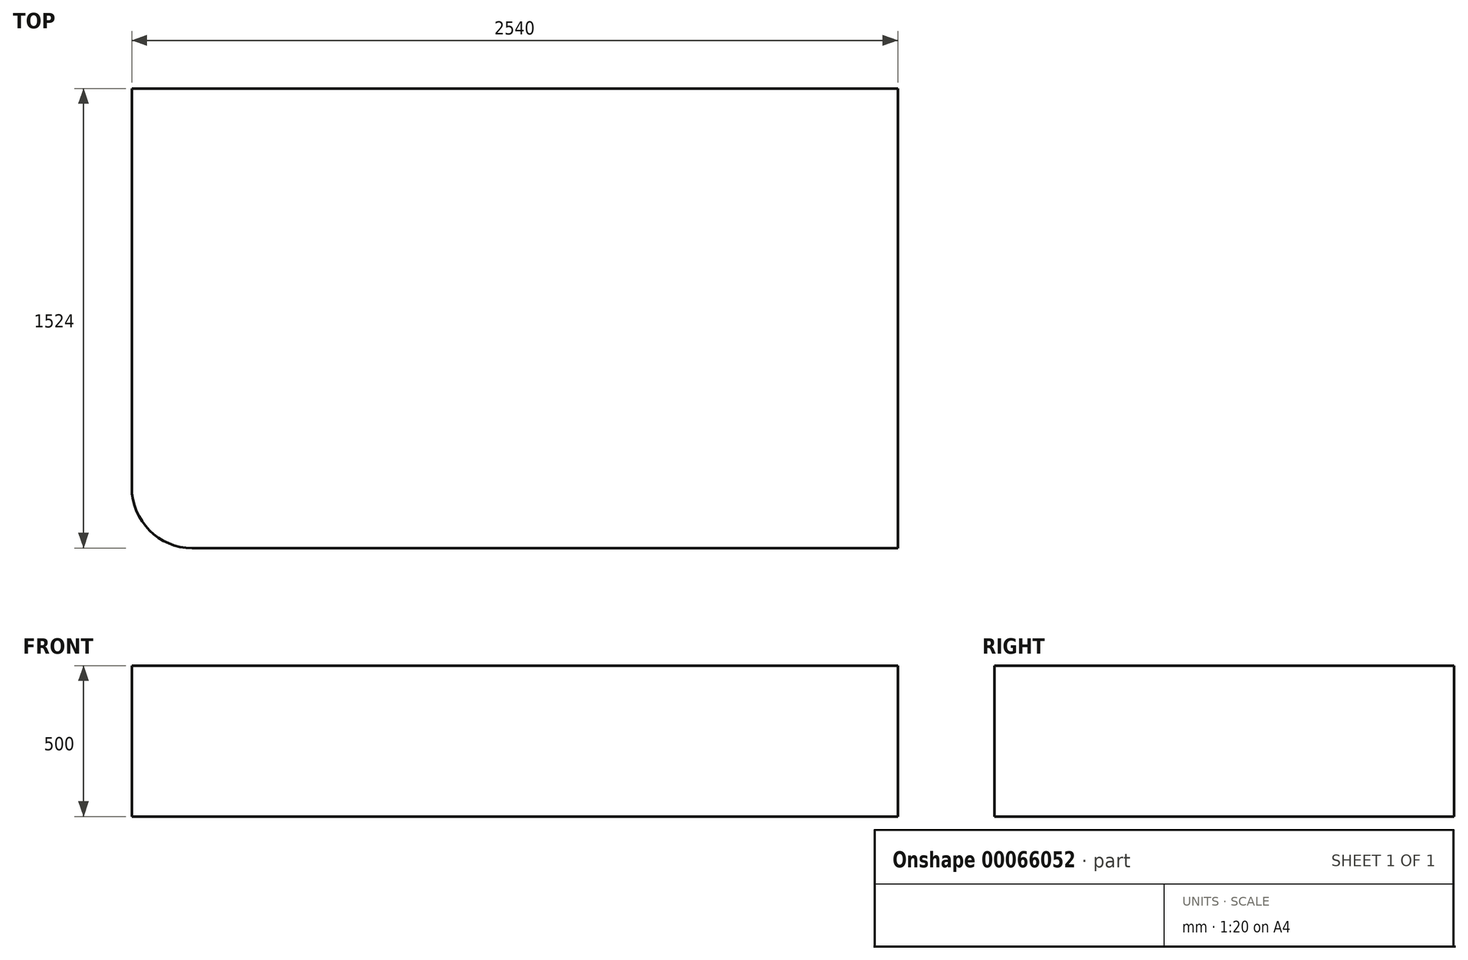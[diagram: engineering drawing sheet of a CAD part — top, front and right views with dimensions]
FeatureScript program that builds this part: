
annotation { "Feature Type Name" : "Feature", "Feature Type Description" : "" }
export const myFeature = defineFeature(function(context is Context, id is Id, definition is map)
    precondition{}
    {
        {
            var Q0;
            Q0=qCreatedBy(makeId("Top.planeOp"),FACE);
            var sketch = newSketch(context, id + "F0", { "sketchPlane" : qUnion([Q0])});
            skLineSegment(sketch, "E0.rect.bottom", {"start": v(1270, 762) * mm, "end": v(-1270, 762) * mm});
            skLineSegment(sketch, "E0.rect.top", {"start": v(1270, -762) * mm, "end": v(-1270, -762) * mm});
            skLineSegment(sketch, "E0.rect.left", {"start": v(1270, 762) * mm, "end": v(1270, -762) * mm});
            skLineSegment(sketch, "E0.rect.right", {"start": v(-1270, 762) * mm, "end": v(-1270, -762) * mm});
            skPoint(sketch, "E0.rect.middle", {"position": v(0, 0) * mm});
            skSolve(sketch);
        }
        {
            var Q0;
            Q0=makeQuery(id+"F0.imprint","IMPRINT",FACE,{"disambiguationData":[TD([[makeQuery(id+"F0.imprint","IMPRINT",EDGE,{"derivedFrom":sQuery(id+"F0.wireOp",EDGE,"E0.rect.bottom")}),1.0]])]});
            extrude(context, id + "F1", {"entities" : qUnion([Q0]), "depth" : 500 * mm});
        }
        {
            var Q0;
            Q0=makeQuery(id+"F1.opExtrude","SWEPT_EDGE",EDGE,{"disambiguationData":[OSD([sQuery(id+"F0.wireOp",EDGE,"E0.rect.top"),sQuery(id+"F0.wireOp",EDGE,"E0.rect.right")])]});
            fillet(context, id + "F2", {"entities" : qUnion([Q0]), "radius" : 200 * mm, "tangentPropagation" : true, "allowEdgeOverflow" : false});
        }
    });
